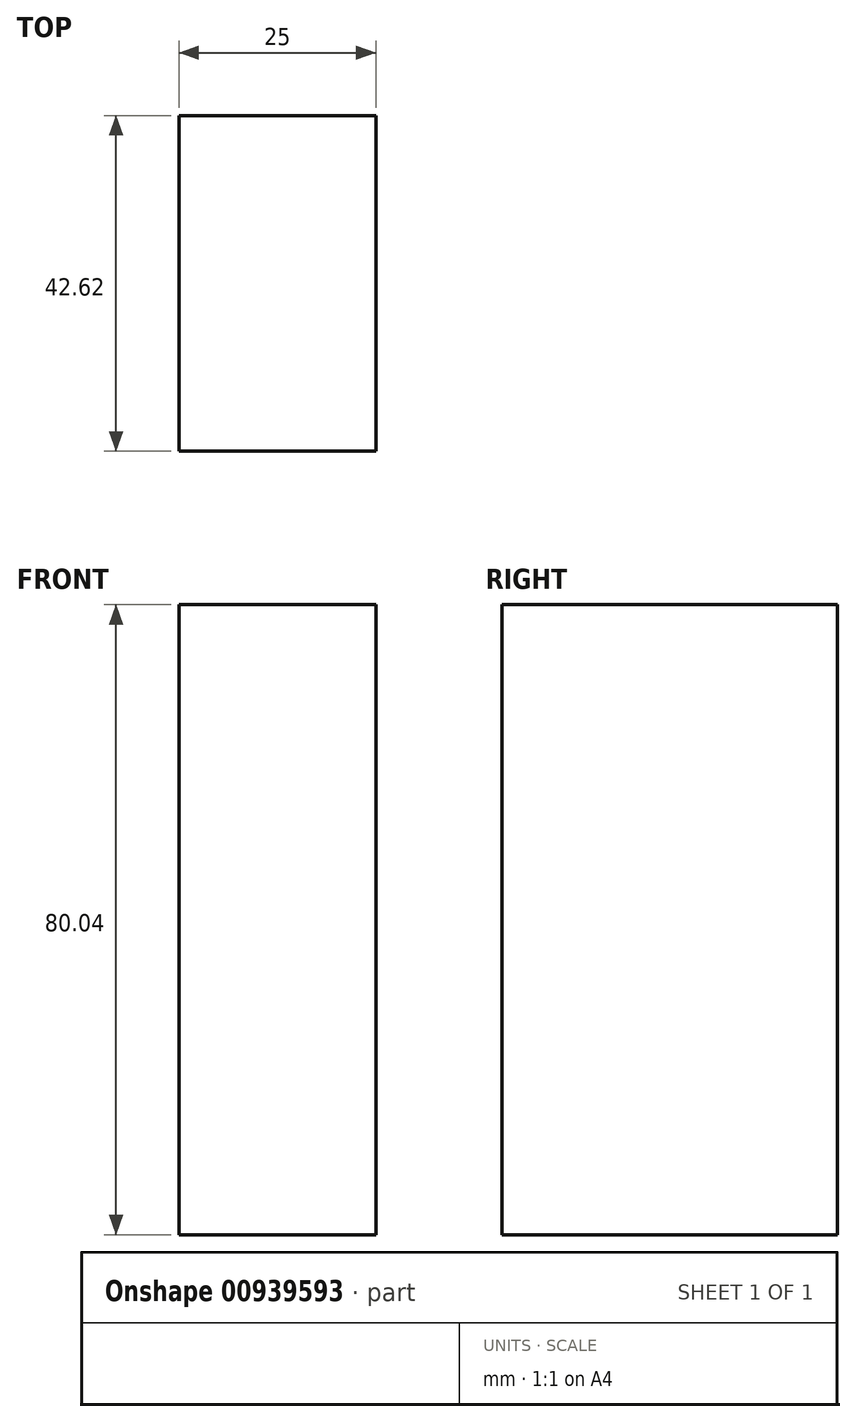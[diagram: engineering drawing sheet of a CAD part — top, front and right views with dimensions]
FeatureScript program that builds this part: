
annotation { "Feature Type Name" : "Feature", "Feature Type Description" : "" }
export const myFeature = defineFeature(function(context is Context, id is Id, definition is map)
    precondition{}
    {
        {
            var Q0;
            Q0=qCreatedBy(makeId("Right.planeOp"),FACE);
            var sketch = newSketch(context, id + "F0", { "sketchPlane" : qUnion([Q0])});
            skLineSegment(sketch, "E0.bottom", {"start": v(74.17, 41.66) * mm, "end": v(31.55, 41.66) * mm});
            skLineSegment(sketch, "E0.top", {"start": v(74.17, -38.38) * mm, "end": v(31.55, -38.38) * mm});
            skLineSegment(sketch, "E0.left", {"start": v(74.17, 41.66) * mm, "end": v(74.17, -38.38) * mm});
            skLineSegment(sketch, "E0.right", {"start": v(31.55, 41.66) * mm, "end": v(31.55, -38.38) * mm});
            skSolve(sketch);
        }
        {
            var Q0;
            Q0 = qSketchRegion(id + "F0", true);
            extrude(context, id + "F1", {"entities" : qUnion([Q0]), "depth" : 25 * mm, "offsetDistance" : 25 * mm});
        }
    });
